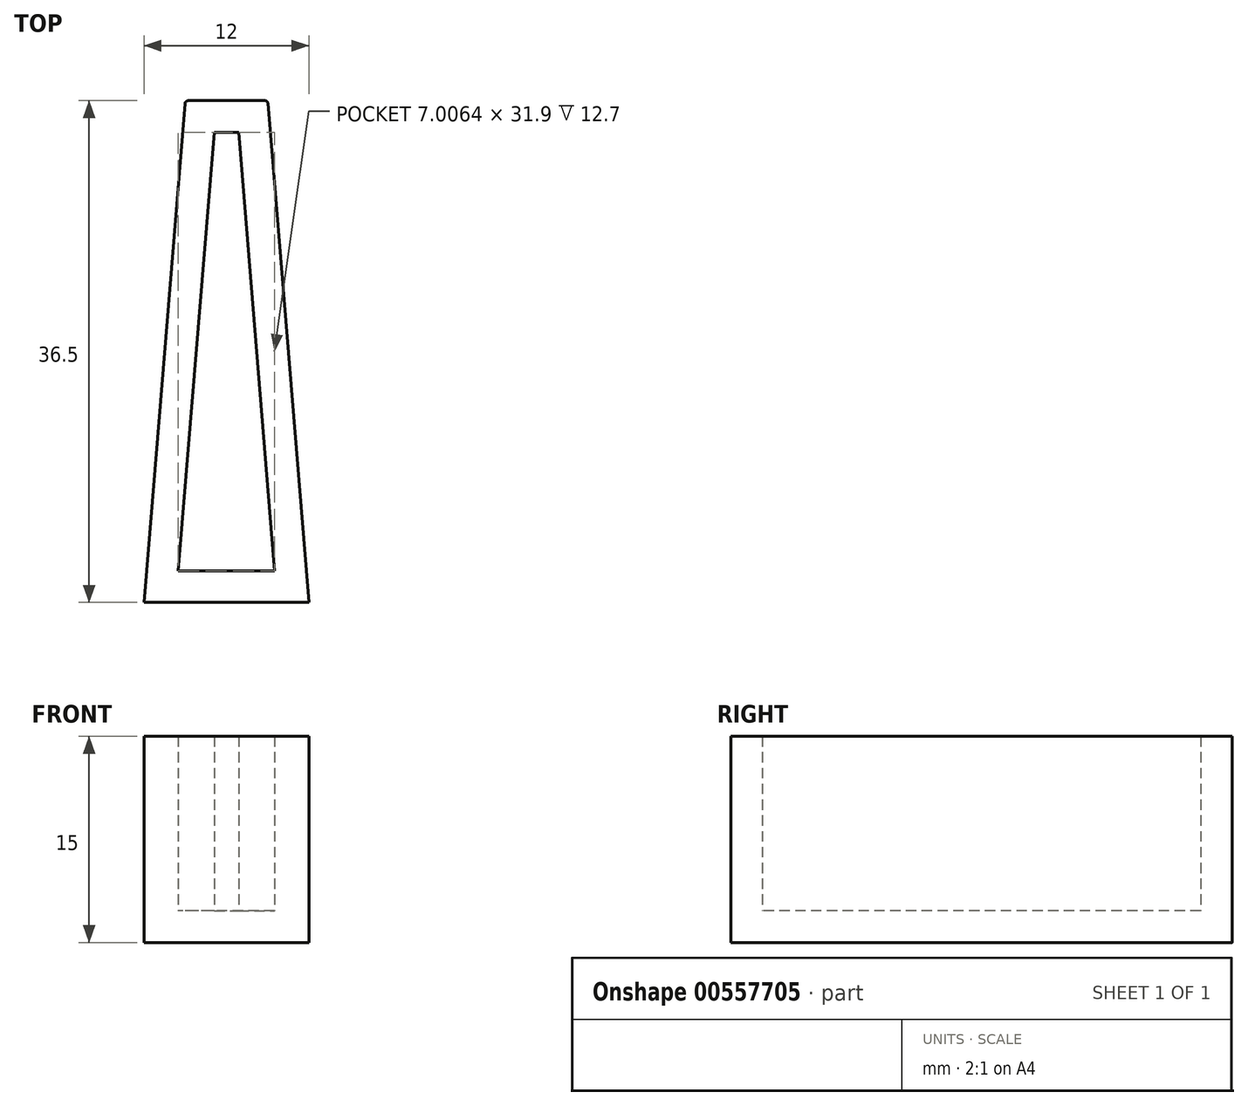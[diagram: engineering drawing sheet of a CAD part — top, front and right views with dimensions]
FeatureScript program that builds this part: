
annotation { "Feature Type Name" : "Feature", "Feature Type Description" : "" }
export const myFeature = defineFeature(function(context is Context, id is Id, definition is map)
    precondition{}
    {
        {
            var Q0;
            Q0=qCreatedBy(makeId("Top.planeOp"),FACE);
            var sketch = newSketch(context, id + "F0", { "sketchPlane" : qUnion([Q0])});
            skPoint(sketch, "E0", {"position": v(0, 36.5) * mm});
            skLineSegment(sketch, "E1", {"start": v(0, 36.5) * mm, "end": v(2.82, 36.5) * mm});
            skLineSegment(sketch, "E2.MirrorCS", {"start": v(0, 36.5) * mm, "end": v(-2.79, 36.5) * mm});
            skLineSegment(sketch, "E3", {"start": v(0, 0) * mm, "end": v(6, 0) * mm});
            skLineSegment(sketch, "E4.MirrorCS", {"start": v(0, 0) * mm, "end": v(-6, 0) * mm});
            skLineSegment(sketch, "E5", {"start": v(3.02, 36.32) * mm, "end": v(6, 0) * mm});
            skLineSegment(sketch, "E6", {"start": v(-3.02, 36.29) * mm, "end": v(-6, 0) * mm});
            skPoint(sketch, "E7.visualSharp", {"position": v(-3, 36.5) * mm});
            skArc(sketch, "E7.filletArc", {"start": v(-2.79, 36.5) * mm, "mid": v(-2.94, 36.44) * mm, "end": v(-3.02, 36.29) * mm});
            skPoint(sketch, "E8.visualSharp", {"position": v(3, 36.5) * mm});
            skArc(sketch, "E8.filletArc", {"start": v(3.02, 36.32) * mm, "mid": v(2.95, 36.45) * mm, "end": v(2.82, 36.5) * mm});
            skSolve(sketch);
        }
        {
            var Q0;
            Q0=qSketchRegion(id+"F0",true);
            extrude(context, id + "F1", {"entities" : qUnion([Q0]), "depth" : 15 * mm, "offsetDistance" : 25 * mm});
        }
        {
            var Q0;
            Q0=makeQuery(id+"F1.opExtrude","CAP_FACE",FACE,{"disambiguationData":[OSD([sQuery(id+"F0.wireOp",EDGE,"E1"),sQuery(id+"F0.wireOp",EDGE,"E2.MirrorCS"),sQuery(id+"F0.wireOp",EDGE,"E3"),sQuery(id+"F0.wireOp",EDGE,"E4.MirrorCS"),sQuery(id+"F0.wireOp",EDGE,"E5"),sQuery(id+"F0.wireOp",EDGE,"E6"),sQuery(id+"F0.wireOp",EDGE,"E7.filletArc"),sQuery(id+"F0.wireOp",EDGE,"E8.filletArc")])],"isStart":false});
            shell(context, id + "F2", {"entities" : qUnion([Q0]), "thickness" : 2.3 * mm});
        }
    });
